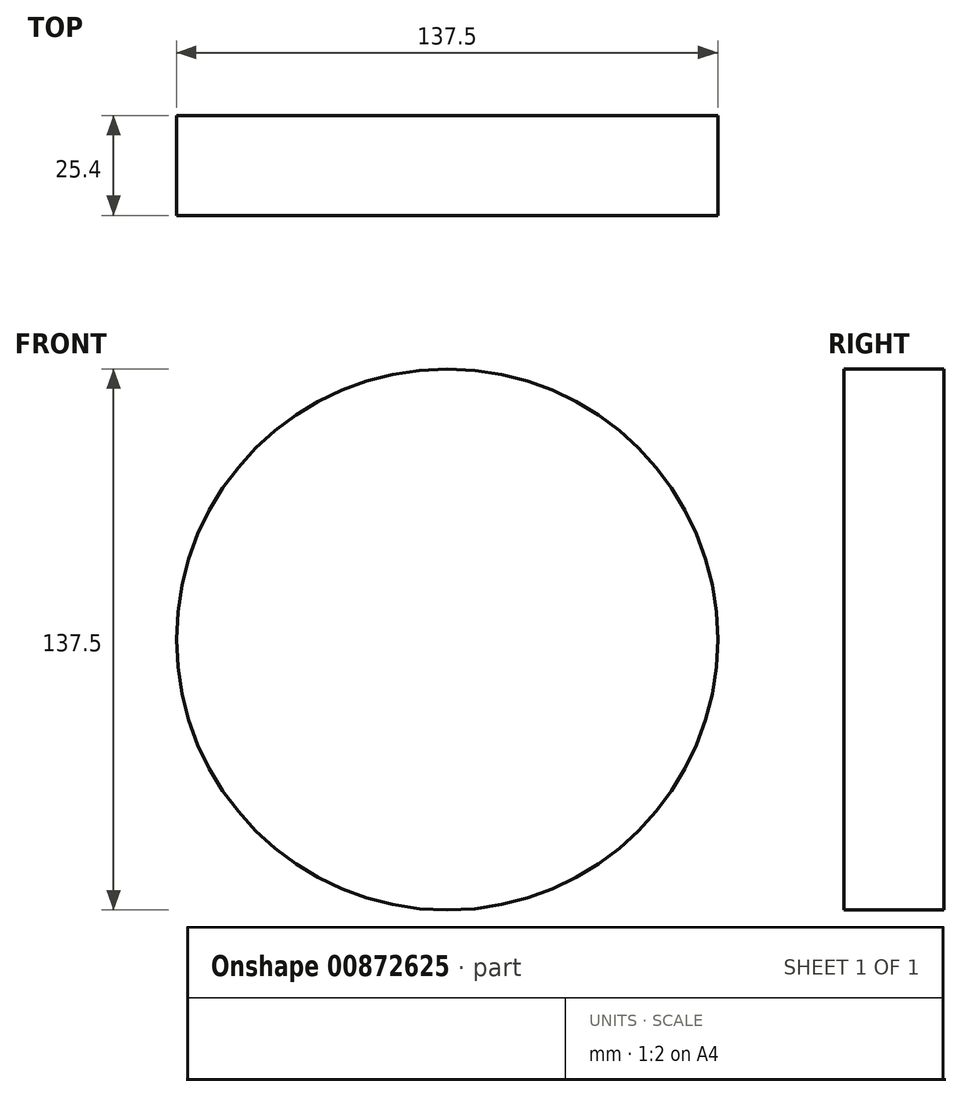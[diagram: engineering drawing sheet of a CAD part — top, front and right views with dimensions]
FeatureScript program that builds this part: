
annotation { "Feature Type Name" : "Feature", "Feature Type Description" : "" }
export const myFeature = defineFeature(function(context is Context, id is Id, definition is map)
    precondition{}
    {
        {
            var Q0;
            Q0=qCreatedBy(makeId("Front.planeOp"),FACE);
            var sketch = newSketch(context, id + "F0", { "sketchPlane" : qUnion([Q0])});
            skCircle(sketch, "E0", {"center": v(0, 0) * mm, "radius": 68.75 * mm});
            skSolve(sketch);
        }
        {
            var Q0;
            Q0 = qSketchRegion(id + "F0", true);
            extrude(context, id + "F1", {"entities" : qUnion([Q0]), "depth" : 25.4 * mm, "offsetDistance" : 25.4 * mm});
        }
    });
